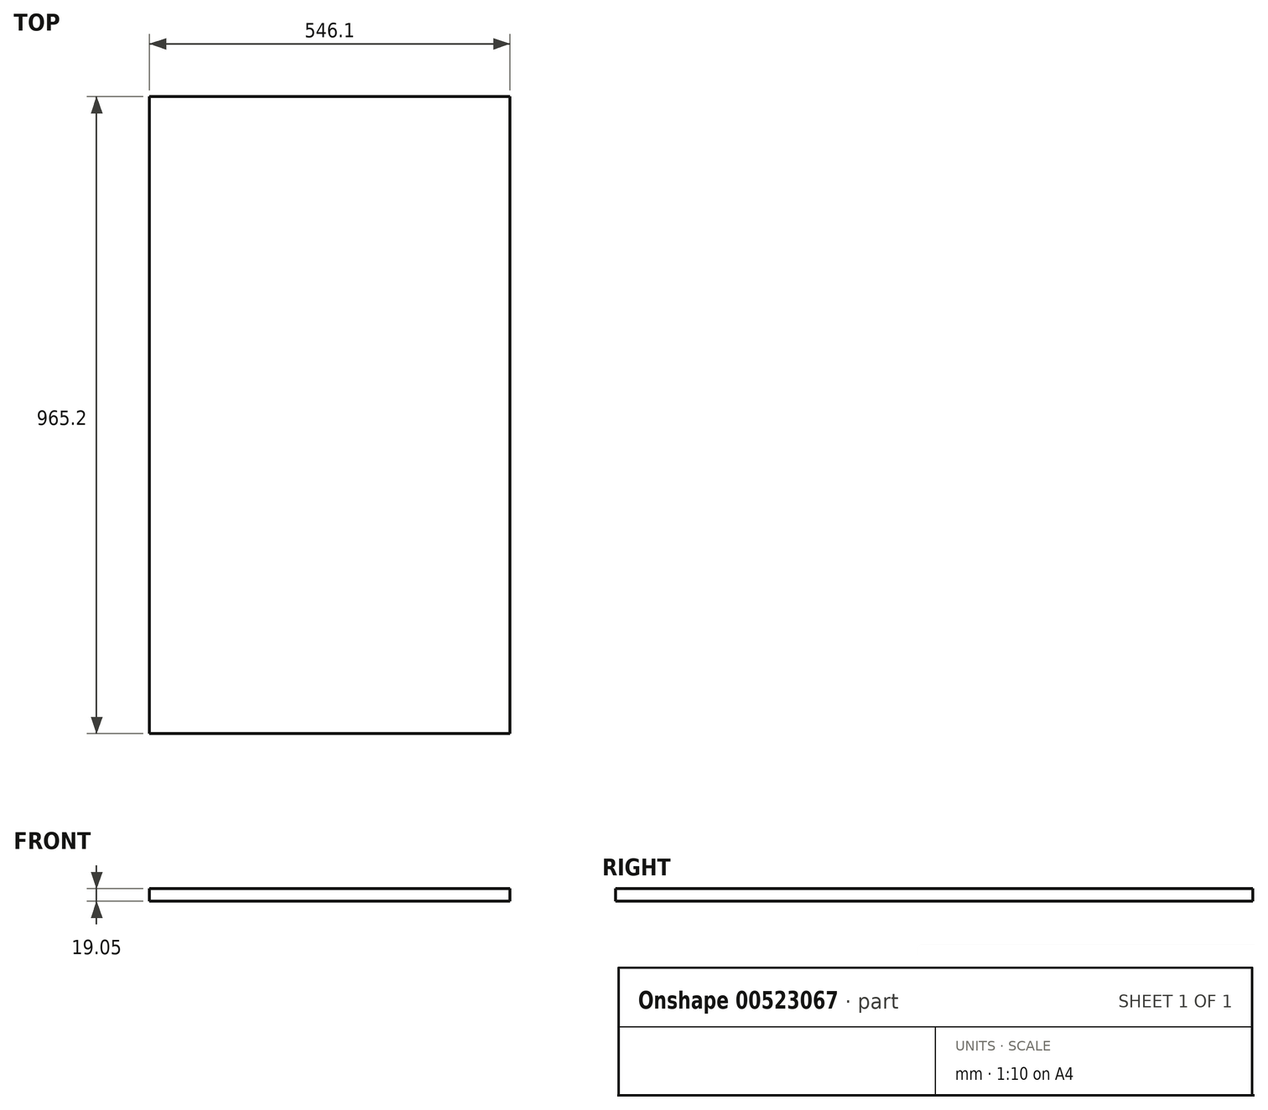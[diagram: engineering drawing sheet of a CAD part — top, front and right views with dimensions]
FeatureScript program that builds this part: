
annotation { "Feature Type Name" : "Feature", "Feature Type Description" : "" }
export const myFeature = defineFeature(function(context is Context, id is Id, definition is map)
    precondition{}
    {
        {
            var Q0;
            Q0=qCreatedBy(makeId("Top.planeOp"),FACE);
            var sketch = newSketch(context, id + "F0", { "sketchPlane" : qUnion([Q0])});
            skLineSegment(sketch, "E0.bottom", {"start": v(0, 0) * mm, "end": v(546.1, 0) * mm});
            skLineSegment(sketch, "E0.top", {"start": v(0, 965.2) * mm, "end": v(546.1, 965.2) * mm});
            skLineSegment(sketch, "E0.left", {"start": v(0, 0) * mm, "end": v(0, 965.2) * mm});
            skLineSegment(sketch, "E0.right", {"start": v(546.1, 0) * mm, "end": v(546.1, 965.2) * mm});
            skSolve(sketch);
        }
        {
            var Q0;
            Q0=qSketchRegion(id+"F0",true);
            extrude(context, id + "F1", {"entities" : qUnion([Q0]), "depth" : 19.05 * mm, "offsetDistance" : 25.4 * mm});
        }
    });
